# Revit family: Sink-Self_Rimming-KOHLER-Ellipse-K-2886X_1
name_source: partatom
category: Plumbing Fixtures
revit_build: Autodesk Revit 2017 (Build: 20160225_1515(x64)
units: mm (PartAtom-declared; Revit-internal decimal feet)

## family parameters
Cut with Voids When Loaded = No
Host = Face
OmniClass Number = 23.31.13.00
OmniClass Title = Sinks
Part Type = Normal
Room Calculation Point = No
Round Connector Dimension = Use Diameter
Shared = No

## types (2) — shared parameters
ADA Compliant = No
Assembly Code = D2010400
CW Connection = No
Cold Water Inlet = Cold Water Inlet
Date Modified = 04/24/2021
Default Elevation = 36"
Description = Counter top cast iron washbasin
Drain Included = No
Finish = Kohler-Vitreous_China-0-White
HW Connection = No
Height = 8 3/8"
Hot Water Inlet = Hot Water Inlet
Length = 19"
Manufacturer = KOHLER Co.
Master Format 2014 = 22 41 16
Master Format 2014 Name = Residential Lavatories and Sinks
Material = Viterious China
Product Documentation Link = http://resources.kohler.com
Product Name = Ellipse
Product Page URL = https://www.kohler.co.th
URL = https://www.kohler.co.th
Vent Connection = No
Waste Connection = Yes
Waste Water Outlet = Waste Water Outlet
WaterSense Certified = No
Width = 33"

## per-type parameters (varying)
| type | Model | Single Hole | Tripal Hole | Type | faucet Hole spacing |
| Single Faucet Hole-0-White | K-2886X-1-0 | Yes | No | 2 | 0" |
| 8 Inch Center Faucet Hole-0-White | K-2886X-8-0 | No | Yes | 1 | 8" |

## geometry (parser evidence)
native form markers: Sweep x5
no freeform markers — native parametric forms only
